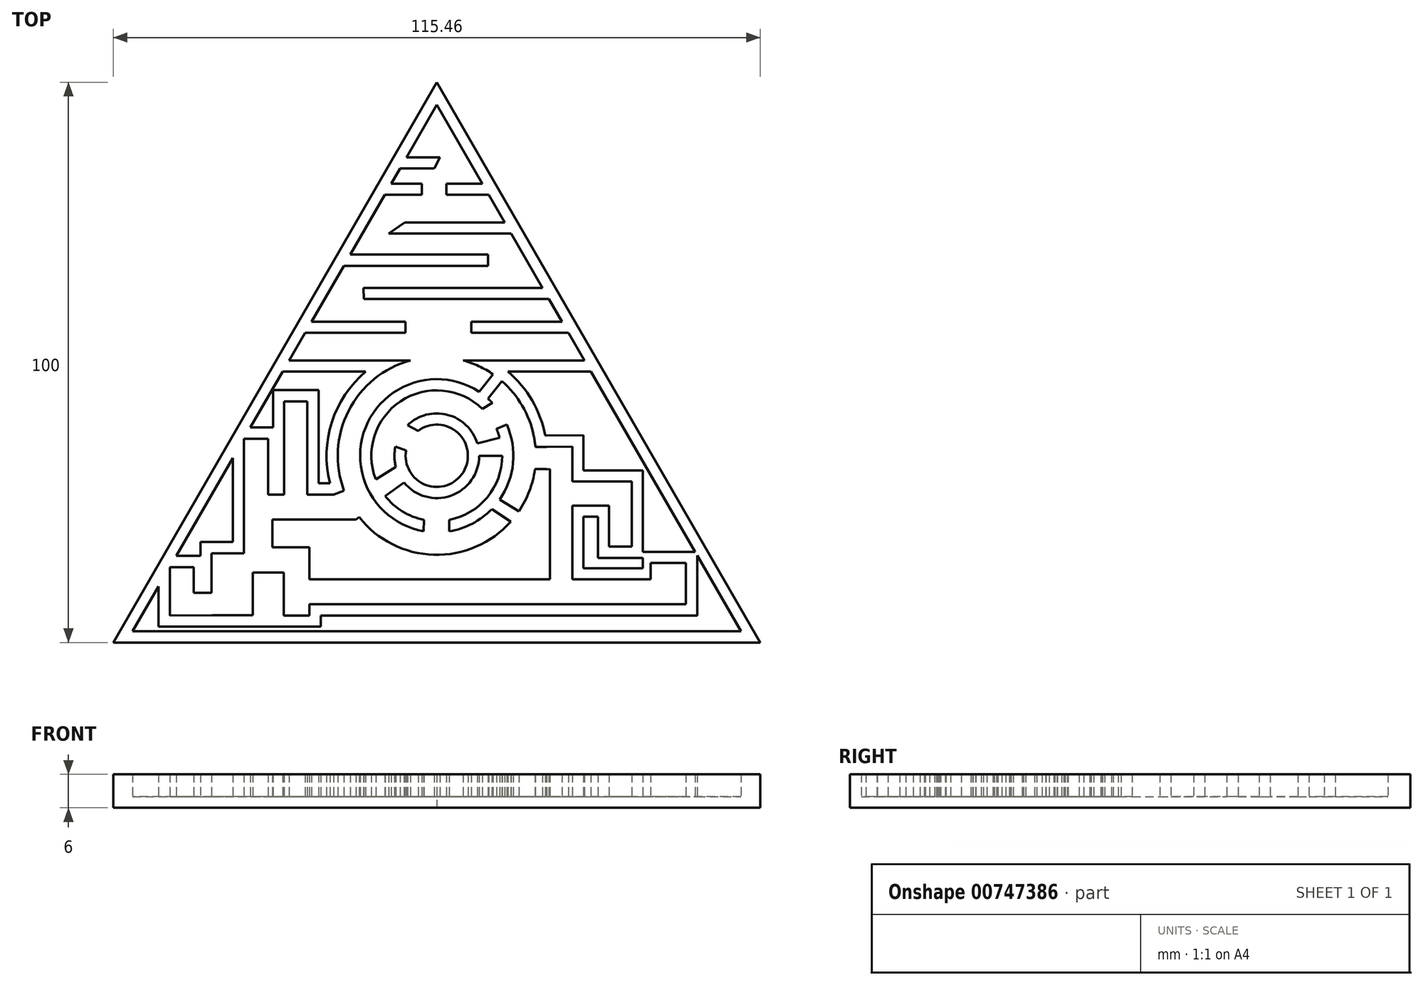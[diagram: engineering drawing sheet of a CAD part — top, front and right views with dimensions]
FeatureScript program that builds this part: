
annotation { "Feature Type Name" : "Feature", "Feature Type Description" : "" }
export const myFeature = defineFeature(function(context is Context, id is Id, definition is map)
    precondition{}
    {
        {
            var Q0;
            Q0=qCreatedBy(makeId("Top.planeOp"),FACE);
            var sketch = newSketch(context, id + "F0", { "sketchPlane" : qUnion([Q0])});
            skLineSegment(sketch, "E0.0", {"start": v(0, 66.66) * mm, "end": v(57.73, -33.34) * mm});
            skLineSegment(sketch, "E0.1", {"start": v(57.73, -33.34) * mm, "end": v(-57.73, -33.34) * mm});
            skLineSegment(sketch, "E0.2", {"start": v(-57.73, -33.34) * mm, "end": v(0, 66.66) * mm});
            skLineSegment(sketch, "E1.0", {"start": v(-54.26, -31.34) * mm, "end": v(-49.65, -23.35) * mm});
            skLineSegment(sketch, "E1.1", {"start": v(54.26, -31.34) * mm, "end": v(-54.26, -31.34) * mm});
            skLineSegment(sketch, "E1.2", {"start": v(0, 62.66) * mm, "end": v(8.12, 48.6) * mm});
            skLineSegment(sketch, "E2", {"start": v(-5.41, 53.28) * mm, "end": v(0.55, 53.28) * mm});
            skLineSegment(sketch, "E3.0", {"start": v(-5.31, 51.28) * mm, "end": v(-0.47, 51.28) * mm});
            skLineSegment(sketch, "E4", {"start": v(8.12, 48.6) * mm, "end": v(1.73, 48.6) * mm});
            skLineSegment(sketch, "E5", {"start": v(-2.68, 48.6) * mm, "end": v(-8.12, 48.6) * mm});
            skLineSegment(sketch, "E6.0", {"start": v(-2.68, 46.6) * mm, "end": v(-8.12, 46.6) * mm});
            skLineSegment(sketch, "E6.2", {"start": v(8.12, 46.6) * mm, "end": v(1.73, 46.6) * mm});
            skLineSegment(sketch, "E7", {"start": v(12.12, 41.67) * mm, "end": v(-5.72, 41.67) * mm});
            skLineSegment(sketch, "E8.0", {"start": v(12.06, 39.67) * mm, "end": v(-8.59, 39.67) * mm});
            skLineSegment(sketch, "E9", {"start": v(-15.45, 35.9) * mm, "end": v(9.13, 35.9) * mm});
            skLineSegment(sketch, "E10.0", {"start": v(-15.45, 33.9) * mm, "end": v(9.13, 33.9) * mm});
            skLineSegment(sketch, "E11", {"start": v(-15.45, 33.9) * mm, "end": v(-16.6, 33.9) * mm});
            skLineSegment(sketch, "E12", {"start": v(12.06, 39.67) * mm, "end": v(13.27, 39.67) * mm});
            skLineSegment(sketch, "E13", {"start": v(-8.59, 39.67) * mm, "end": v(-5.72, 41.67) * mm});
            skLineSegment(sketch, "E14", {"start": v(-2.68, 46.6) * mm, "end": v(-2.68, 48.6) * mm});
            skLineSegment(sketch, "E15", {"start": v(1.73, 48.6) * mm, "end": v(1.73, 46.6) * mm});
            skLineSegment(sketch, "E16", {"start": v(8.12, 46.6) * mm, "end": v(9.27, 46.6) * mm});
            skLineSegment(sketch, "E17", {"start": v(-8.12, 46.6) * mm, "end": v(-9.27, 46.6) * mm});
            skLineSegment(sketch, "E18", {"start": v(-5.31, 51.28) * mm, "end": v(-6.57, 51.28) * mm});
            skLineSegment(sketch, "E19", {"start": v(-0.47, 51.28) * mm, "end": v(0.55, 53.28) * mm});
            skLineSegment(sketch, "E20", {"start": v(9.13, 35.9) * mm, "end": v(9.13, 33.9) * mm});
            skLineSegment(sketch, "E21", {"start": v(18.87, 29.98) * mm, "end": v(-13.07, 29.98) * mm});
            skLineSegment(sketch, "E22.0", {"start": v(18.7, 27.98) * mm, "end": v(-13.01, 27.98) * mm});
            skLineSegment(sketch, "E23", {"start": v(-13.07, 29.98) * mm, "end": v(-13.01, 27.98) * mm});
            skLineSegment(sketch, "E24", {"start": v(18.7, 27.98) * mm, "end": v(20.02, 27.98) * mm});
            skArc(sketch, "E25", {"start": v(-4.71, 17.03) * mm, "mid": v(-7.07, 16.2) * mm, "end": v(-9.3, 15.03) * mm});
            skLineSegment(sketch, "E26", {"start": v(-22.35, 23.94) * mm, "end": v(-5.6, 23.94) * mm});
            skLineSegment(sketch, "E27", {"start": v(6.16, 23.94) * mm, "end": v(22.35, 23.94) * mm});
            skLineSegment(sketch, "E28.0", {"start": v(-22.35, 21.94) * mm, "end": v(-5.6, 21.94) * mm});
            skLineSegment(sketch, "E29.0", {"start": v(6.16, 21.94) * mm, "end": v(22.35, 21.94) * mm});
            skLineSegment(sketch, "E30", {"start": v(-5.6, 21.94) * mm, "end": v(-5.6, 23.94) * mm});
            skLineSegment(sketch, "E31", {"start": v(6.16, 23.94) * mm, "end": v(6.16, 21.94) * mm});
            skLineSegment(sketch, "E32", {"start": v(22.35, 21.94) * mm, "end": v(23.5, 21.94) * mm});
            skLineSegment(sketch, "E33", {"start": v(-22.35, 21.94) * mm, "end": v(-23.5, 21.94) * mm});
            skLineSegment(sketch, "E34", {"start": v(-26.34, 17.03) * mm, "end": v(-4.71, 17.03) * mm});
            skLineSegment(sketch, "E35", {"start": v(4.71, 17.03) * mm, "end": v(26.34, 17.03) * mm});
            skLineSegment(sketch, "E36.0", {"start": v(-26.34, 15.03) * mm, "end": v(-12.7, 15.03) * mm});
            skLineSegment(sketch, "E37.0", {"start": v(12.7, 15.03) * mm, "end": v(26.34, 15.03) * mm});
            skLineSegment(sketch, "E38", {"start": v(-26.34, 15.03) * mm, "end": v(-27.5, 15.03) * mm});
            skLineSegment(sketch, "E39", {"start": v(26.34, 15.03) * mm, "end": v(27.5, 15.03) * mm});
            skLineSegment(sketch, "E40.trimOffspring", {"start": v(-15.45, 35.9) * mm, "end": v(-9.27, 46.6) * mm});
            skLineSegment(sketch, "E41.trimOffspring", {"start": v(13.27, 39.67) * mm, "end": v(18.87, 29.98) * mm});
            skLineSegment(sketch, "E42.trimOffspring", {"start": v(20.02, 27.98) * mm, "end": v(22.35, 23.94) * mm});
            skLineSegment(sketch, "E43.trimOffspring", {"start": v(-26.34, 17.03) * mm, "end": v(-23.5, 21.94) * mm});
            skLineSegment(sketch, "E44.trimOffspring", {"start": v(-22.35, 23.94) * mm, "end": v(-16.6, 33.9) * mm});
            skLineSegment(sketch, "E45.trimOffspring", {"start": v(27.5, 15.03) * mm, "end": v(46.07, -17.15) * mm});
            skLineSegment(sketch, "E46.trimOffspring", {"start": v(23.5, 21.94) * mm, "end": v(26.34, 17.03) * mm});
            skLineSegment(sketch, "E47.trimOffspring", {"start": v(-8.12, 48.6) * mm, "end": v(-6.57, 51.28) * mm});
            skLineSegment(sketch, "E48.trimOffspring", {"start": v(9.27, 46.6) * mm, "end": v(12.12, 41.67) * mm});
            skLineSegment(sketch, "E49.trimOffspring", {"start": v(-5.41, 53.28) * mm, "end": v(0, 62.66) * mm});
            skArc(sketch, "E50.trimOffspring", {"start": v(9.3, 15.03) * mm, "mid": v(7.07, 16.2) * mm, "end": v(4.71, 17.03) * mm});
            skArc(sketch, "E51", {"start": v(-4.71, 17.03) * mm, "mid": v(-15.75, 8.02) * mm, "end": v(-16.54, -6.22) * mm});
            skArc(sketch, "E52.0", {"start": v(7.52, 11.42) * mm, "mid": v(-12.72, 5.03) * mm, "end": v(-2.32, -13.48) * mm});
            skArc(sketch, "E53.0", {"start": v(2.2, -11.47) * mm, "mid": v(9, -7.44) * mm, "end": v(11.67, 0) * mm});
            skArc(sketch, "E54.0", {"start": v(7.23, 2.22) * mm, "mid": v(1.91, 7.31) * mm, "end": v(-5.21, 5.47) * mm});
            skArc(sketch, "E55.0", {"start": v(-5.48, 0.95) * mm, "mid": v(4.73, -2.91) * mm, "end": v(-3.32, 4.46) * mm});
            skArc(sketch, "E56.0", {"start": v(-12.7, 15.03) * mm, "mid": v(-18.74, 5.98) * mm, "end": v(-19.05, -4.9) * mm});
            skLineSegment(sketch, "E57", {"start": v(7.52, 11.42) * mm, "end": v(10.06, 14.53) * mm});
            skLineSegment(sketch, "E58.0", {"start": v(10.67, 12.12) * mm, "end": v(11.63, 13.3) * mm});
            skLineSegment(sketch, "E59", {"start": v(10.67, 12.12) * mm, "end": v(9.13, 10.18) * mm});
            skArc(sketch, "E60.trimOffspring", {"start": v(10.06, 14.53) * mm, "mid": v(7.49, 16) * mm, "end": v(4.71, 17.03) * mm});
            skLineSegment(sketch, "E61.left", {"start": v(-2.32, -11.44) * mm, "end": v(-2.32, -13.48) * mm});
            skLineSegment(sketch, "E61.right", {"start": v(2.2, -11.47) * mm, "end": v(2.19, -13.5) * mm});
            skArc(sketch, "E62.trimOffspring", {"start": v(2.19, -13.5) * mm, "mid": v(6.32, -12.12) * mm, "end": v(9.82, -9.52) * mm});
            skLineSegment(sketch, "E63", {"start": v(-9.2, -7.18) * mm, "end": v(-5.86, -4.77) * mm});
            skLineSegment(sketch, "E64", {"start": v(-10.88, -4.22) * mm, "end": v(-7.3, -1.99) * mm});
            skLineSegment(sketch, "E65", {"start": v(7.23, 2.22) * mm, "end": v(11.23, 3.2) * mm});
            skLineSegment(sketch, "E66", {"start": v(7.56, 0) * mm, "end": v(11.67, 0) * mm});
            skArc(sketch, "E67.trimOffspring", {"start": v(11.23, 3.2) * mm, "mid": v(10.97, 4) * mm, "end": v(10.65, 4.79) * mm});
            skArc(sketch, "E68.trimOffspring", {"start": v(-5.86, -4.77) * mm, "mid": v(2.53, -7.12) * mm, "end": v(7.56, 0) * mm});
            skArc(sketch, "E69.trimOffspring", {"start": v(-9.2, -7.18) * mm, "mid": v(-6.14, -9.93) * mm, "end": v(-2.32, -11.44) * mm});
            skArc(sketch, "E70.trimOffspring", {"start": v(-13.87, -10.96) * mm, "mid": v(-0.52, -17.67) * mm, "end": v(13.2, -11.75) * mm});
            skLineSegment(sketch, "E71", {"start": v(-18.42, -6.9) * mm, "end": v(-16.54, -6.22) * mm});
            skLineSegment(sketch, "E72", {"start": v(-18.42, -6.9) * mm, "end": v(-23.1, -6.9) * mm});
            skLineSegment(sketch, "E73", {"start": v(-23.1, -6.9) * mm, "end": v(-23.1, 9.73) * mm});
            skLineSegment(sketch, "E74", {"start": v(-23.1, 9.73) * mm, "end": v(-27.23, 9.73) * mm});
            skLineSegment(sketch, "E75", {"start": v(-27.23, 9.73) * mm, "end": v(-27.23, -6.9) * mm});
            skLineSegment(sketch, "E76", {"start": v(-27.23, -6.9) * mm, "end": v(-30.11, -6.9) * mm});
            skLineSegment(sketch, "E77", {"start": v(-30.11, -6.9) * mm, "end": v(-30.11, 3.06) * mm});
            skLineSegment(sketch, "E78", {"start": v(-30.11, 3.06) * mm, "end": v(-34.4, 3.06) * mm});
            skLineSegment(sketch, "E79", {"start": v(-34.4, 3.06) * mm, "end": v(-34.4, -6.9) * mm});
            skLineSegment(sketch, "E80", {"start": v(-34.4, -6.9) * mm, "end": v(-34.4, -13.59) * mm});
            skLineSegment(sketch, "E81", {"start": v(-34.4, -13.59) * mm, "end": v(-34.4, -17.39) * mm});
            skLineSegment(sketch, "E82", {"start": v(-34.4, -17.39) * mm, "end": v(-40.19, -17.39) * mm});
            skLineSegment(sketch, "E83", {"start": v(-40.19, -17.39) * mm, "end": v(-40.19, -24.18) * mm});
            skLineSegment(sketch, "E84", {"start": v(-40.19, -24.18) * mm, "end": v(-40.19, -24.46) * mm});
            skLineSegment(sketch, "E85", {"start": v(-40.19, -24.46) * mm, "end": v(-43.4, -24.46) * mm});
            skLineSegment(sketch, "E86", {"start": v(-43.4, -24.46) * mm, "end": v(-43.4, -19.89) * mm});
            skLineSegment(sketch, "E87", {"start": v(-43.4, -19.89) * mm, "end": v(-47.65, -19.89) * mm});
            skLineSegment(sketch, "E88", {"start": v(-47.65, -19.89) * mm, "end": v(-47.65, -24.46) * mm});
            skLineSegment(sketch, "E89", {"start": v(-47.65, -24.46) * mm, "end": v(-47.65, -28.51) * mm});
            skLineSegment(sketch, "E90", {"start": v(-47.65, -28.51) * mm, "end": v(-40.09, -28.47) * mm});
            skLineSegment(sketch, "E91", {"start": v(-40.09, -28.47) * mm, "end": v(-32.84, -28.47) * mm});
            skLineSegment(sketch, "E92", {"start": v(-32.84, -28.47) * mm, "end": v(-32.84, -20.83) * mm});
            skLineSegment(sketch, "E93", {"start": v(-32.84, -20.83) * mm, "end": v(-27.33, -20.83) * mm});
            skLineSegment(sketch, "E94", {"start": v(-27.33, -20.83) * mm, "end": v(-27.33, -28.5) * mm});
            skLineSegment(sketch, "E95", {"start": v(-27.33, -28.5) * mm, "end": v(-22.71, -28.5) * mm});
            skLineSegment(sketch, "E96", {"start": v(-22.71, -28.5) * mm, "end": v(-22.71, -26.53) * mm});
            skLineSegment(sketch, "E97", {"start": v(-22.71, -20.74) * mm, "end": v(-22.71, -16.35) * mm});
            skLineSegment(sketch, "E98", {"start": v(-22.71, -16.35) * mm, "end": v(-29.3, -16.35) * mm});
            skLineSegment(sketch, "E99", {"start": v(-29.3, -16.35) * mm, "end": v(-29.3, -11.37) * mm});
            skLineSegment(sketch, "E100", {"start": v(-29.3, -11.37) * mm, "end": v(-24.62, -11.37) * mm});
            skLineSegment(sketch, "E101", {"start": v(-14.4, -11.37) * mm, "end": v(-13.87, -10.96) * mm});
            skLineSegment(sketch, "E102.0", {"start": v(-21.1, -4.9) * mm, "end": v(-21.1, 9.73) * mm});
            skLineSegment(sketch, "E103.0", {"start": v(-23.1, 11.73) * mm, "end": v(-27.23, 11.73) * mm});
            skLineSegment(sketch, "E104.top", {"start": v(-23.1, 11.71) * mm, "end": v(-21.11, 11.71) * mm});
            skLineSegment(sketch, "E104.right", {"start": v(-21.11, 9.73) * mm, "end": v(-21.11, 11.71) * mm});
            skLineSegment(sketch, "E105.0", {"start": v(-29.23, 9.73) * mm, "end": v(-29.23, 5.06) * mm});
            skLineSegment(sketch, "E106.top", {"start": v(-29.23, 11.73) * mm, "end": v(-27.23, 11.73) * mm});
            skLineSegment(sketch, "E106.left", {"start": v(-29.23, 9.73) * mm, "end": v(-29.23, 11.73) * mm});
            skLineSegment(sketch, "E107.0", {"start": v(-30.11, 5.06) * mm, "end": v(-33.25, 5.06) * mm});
            skLineSegment(sketch, "E108.bottom", {"start": v(-30.11, 5.06) * mm, "end": v(-29.23, 5.06) * mm});
            skLineSegment(sketch, "E109.trimOffspring", {"start": v(-33.25, 5.06) * mm, "end": v(-27.5, 15.03) * mm});
            skLineSegment(sketch, "E110.0", {"start": v(-36.4, -13.59) * mm, "end": v(-36.4, -15.39) * mm});
            skLineSegment(sketch, "E110.1", {"start": v(-36.4, -6.9) * mm, "end": v(-36.4, -13.59) * mm});
            skLineSegment(sketch, "E110.2", {"start": v(-36.4, -0.4) * mm, "end": v(-36.4, -6.9) * mm});
            skLineSegment(sketch, "E111.0", {"start": v(-36.4, -15.39) * mm, "end": v(-40.19, -15.39) * mm});
            skLineSegment(sketch, "E112.0", {"start": v(-42.19, -17.39) * mm, "end": v(-42.19, -17.89) * mm});
            skLineSegment(sketch, "E113.top", {"start": v(-42.19, -15.39) * mm, "end": v(-40.19, -15.39) * mm});
            skLineSegment(sketch, "E113.left", {"start": v(-42.19, -17.39) * mm, "end": v(-42.19, -15.39) * mm});
            skLineSegment(sketch, "E114.0", {"start": v(-43.4, -17.89) * mm, "end": v(-46.5, -17.89) * mm});
            skLineSegment(sketch, "E115.bottom", {"start": v(-43.4, -17.89) * mm, "end": v(-42.19, -17.89) * mm});
            skLineSegment(sketch, "E116.0", {"start": v(-49.65, -24.46) * mm, "end": v(-49.65, -28.51) * mm});
            skLineSegment(sketch, "E116.1", {"start": v(-49.65, -23.35) * mm, "end": v(-49.65, -24.46) * mm});
            skLineSegment(sketch, "E117.trimOffspring", {"start": v(-46.5, -17.89) * mm, "end": v(-36.4, -0.4) * mm});
            skLineSegment(sketch, "E118.0", {"start": v(-47.64, -30.5) * mm, "end": v(-40.07, -30.47) * mm});
            skLineSegment(sketch, "E119.bottom", {"start": v(-47.65, -28.51) * mm, "end": v(-47.64, -28.51) * mm});
            skLineSegment(sketch, "E119.top", {"start": v(-49.65, -30.5) * mm, "end": v(-47.64, -30.5) * mm});
            skLineSegment(sketch, "E119.left", {"start": v(-49.65, -28.51) * mm, "end": v(-49.65, -30.5) * mm});
            skLineSegment(sketch, "E120.0", {"start": v(-40.09, -30.47) * mm, "end": v(-32.84, -30.47) * mm});
            skLineSegment(sketch, "E121", {"start": v(-32.84, -30.47) * mm, "end": v(-27.36, -30.47) * mm});
            skLineSegment(sketch, "E122", {"start": v(-27.36, -30.47) * mm, "end": v(-20.88, -30.47) * mm});
            skLineSegment(sketch, "E123.top", {"start": v(-20.88, -30.47) * mm, "end": v(-20.72, -30.47) * mm});
            skLineSegment(sketch, "E123.right", {"start": v(-20.72, -28.5) * mm, "end": v(-20.72, -30.47) * mm});
            skLineSegment(sketch, "E124.0", {"start": v(-19.05, -4.9) * mm, "end": v(-21.1, -4.9) * mm});
            skLineSegment(sketch, "E125", {"start": v(-24.62, -11.37) * mm, "end": v(-20.71, -11.37) * mm});
            skLineSegment(sketch, "E126", {"start": v(-20.7, -13.37) * mm, "end": v(-20.7, -13.37) * mm});
            skPoint(sketch, "E126.endSnap0", {"position": v(-20.7, -13.3) * mm});
            skLineSegment(sketch, "E127", {"start": v(-20.71, -11.37) * mm, "end": v(-14.4, -11.37) * mm});
            skPoint(sketch, "E128.end.orphan", {"position": v(-20.67, -12.27) * mm});
            skLineSegment(sketch, "E129.bottom", {"start": v(-22.71, -22.05) * mm, "end": v(-20.71, -22.05) * mm});
            skLineSegment(sketch, "E129.top", {"start": v(-22.71, -26.53) * mm, "end": v(-20.71, -26.53) * mm});
            skLineSegment(sketch, "E130.trimOffspring", {"start": v(-22.71, -22.05) * mm, "end": v(-22.71, -20.74) * mm});
            skLineSegment(sketch, "E131", {"start": v(-20.71, -26.53) * mm, "end": v(-12.97, -26.53) * mm});
            skLineSegment(sketch, "E132.0", {"start": v(-20.71, -28.53) * mm, "end": v(-12.97, -28.53) * mm});
            skLineSegment(sketch, "E133", {"start": v(-20.71, -22.05) * mm, "end": v(-12.69, -22.05) * mm});
            skLineSegment(sketch, "E134", {"start": v(9.82, -9.52) * mm, "end": v(13.2, -11.75) * mm});
            skLineSegment(sketch, "E135", {"start": v(14.65, -9.89) * mm, "end": v(11.23, -7.8) * mm});
            skLineSegment(sketch, "E136", {"start": v(-12.97, -28.53) * mm, "end": v(18.13, -28.53) * mm});
            skLineSegment(sketch, "E137.0", {"start": v(-12.97, -26.53) * mm, "end": v(18.13, -26.53) * mm});
            skLineSegment(sketch, "E138.0", {"start": v(-12.69, -22.05) * mm, "end": v(18.13, -22.05) * mm});
            skLineSegment(sketch, "E139", {"start": v(18.13, -26.53) * mm, "end": v(24.45, -26.53) * mm});
            skLineSegment(sketch, "E140", {"start": v(24.45, -26.53) * mm, "end": v(44.46, -26.53) * mm});
            skLineSegment(sketch, "E141", {"start": v(44.46, -26.53) * mm, "end": v(44.46, -19.15) * mm});
            skLineSegment(sketch, "E142", {"start": v(44.46, -19.15) * mm, "end": v(38.16, -19.15) * mm});
            skLineSegment(sketch, "E143", {"start": v(38.16, -19.15) * mm, "end": v(38.16, -22.05) * mm});
            skLineSegment(sketch, "E144", {"start": v(38.16, -22.05) * mm, "end": v(24.18, -22.05) * mm});
            skLineSegment(sketch, "E145", {"start": v(18.13, -28.53) * mm, "end": v(46.46, -28.53) * mm});
            skLineSegment(sketch, "E146.0", {"start": v(46.46, -26.53) * mm, "end": v(46.46, -19.15) * mm});
            skLineSegment(sketch, "E147", {"start": v(46.46, -26.53) * mm, "end": v(46.46, -28.53) * mm});
            skLineSegment(sketch, "E148.0", {"start": v(44.46, -17.15) * mm, "end": v(38.16, -17.15) * mm});
            skLineSegment(sketch, "E149.bottom", {"start": v(44.46, -17.15) * mm, "end": v(46.07, -17.15) * mm});
            skLineSegment(sketch, "E149.right", {"start": v(46.46, -17.82) * mm, "end": v(46.46, -19.15) * mm});
            skLineSegment(sketch, "E150.trimOffspring", {"start": v(46.46, -17.82) * mm, "end": v(54.26, -31.34) * mm});
            skLineSegment(sketch, "E151.top", {"start": v(36.8, -17.15) * mm, "end": v(38.16, -17.15) * mm});
            skLineSegment(sketch, "E151.right", {"start": v(38.16, -20.05) * mm, "end": v(38.16, -19.15) * mm});
            skLineSegment(sketch, "E152.left", {"start": v(20.18, -20.05) * mm, "end": v(20.18, -22.05) * mm});
            skLineSegment(sketch, "E152.right", {"start": v(24.18, -20.05) * mm, "end": v(24.18, -22.05) * mm});
            skLineSegment(sketch, "E153.trimOffspring", {"start": v(24.18, -20.05) * mm, "end": v(24.18, -20.05) * mm});
            skLineSegment(sketch, "E154.trimOffspring", {"start": v(20.18, -22.05) * mm, "end": v(18.13, -22.05) * mm});
            skLineSegment(sketch, "E155", {"start": v(20.18, -20.05) * mm, "end": v(20.18, -6.8) * mm});
            skLineSegment(sketch, "E156", {"start": v(20.18, -6.8) * mm, "end": v(20.18, -2.4) * mm});
            skLineSegment(sketch, "E157", {"start": v(20.18, -2.4) * mm, "end": v(19.53, -2.4) * mm});
            skLineSegment(sketch, "E158.0", {"start": v(24.18, 1.65) * mm, "end": v(19.6, 1.6) * mm});
            skLineSegment(sketch, "E158.1", {"start": v(24.18, -4.6) * mm, "end": v(24.18, 1.65) * mm});
            skLineSegment(sketch, "E158.2", {"start": v(24.18, -20.05) * mm, "end": v(24.18, -8.9) * mm});
            skLineSegment(sketch, "E159.0", {"start": v(26.18, 3.68) * mm, "end": v(19.46, 3.6) * mm});
            skLineSegment(sketch, "E159.1", {"start": v(26.18, -2.6) * mm, "end": v(26.18, 3.68) * mm});
            skLineSegment(sketch, "E160", {"start": v(19.46, 3.6) * mm, "end": v(19.34, 3.6) * mm});
            skArc(sketch, "E161.trimOffspring", {"start": v(19.34, 3.6) * mm, "mid": v(17, 9.9) * mm, "end": v(12.7, 15.03) * mm});
            skLineSegment(sketch, "E162.top", {"start": v(19.6, 3.6) * mm, "end": v(19.34, 3.6) * mm});
            skArc(sketch, "E163.trimOffspring", {"start": v(17.3, 3.6) * mm, "mid": v(15.26, 8.92) * mm, "end": v(11.63, 13.3) * mm});
            skLineSegment(sketch, "E164", {"start": v(19.6, 1.6) * mm, "end": v(17.6, 1.6) * mm});
            skArc(sketch, "E165.trimOffspring", {"start": v(19.53, -2.4) * mm, "mid": v(19.53, -2.4) * mm, "end": v(19.53, -2.4) * mm});
            skLineSegment(sketch, "E166.bottom", {"start": v(20.18, -2.4) * mm, "end": v(17.51, -2.4) * mm});
            skLineSegment(sketch, "E166.top", {"start": v(20.18, 1.6) * mm, "end": v(17.6, 1.6) * mm});
            skArc(sketch, "E167", {"start": v(17.6, 1.6) * mm, "mid": v(17.48, 2.6) * mm, "end": v(17.3, 3.6) * mm});
            skArc(sketch, "E168.trimOffspring", {"start": v(8.13, 8.38) * mm, "mid": v(-6.45, 9.73) * mm, "end": v(-10.88, -4.22) * mm});
            skArc(sketch, "E169.trimOffspring", {"start": v(9.91, 9.42) * mm, "mid": v(9.53, 9.8) * mm, "end": v(9.13, 10.18) * mm});
            skLineSegment(sketch, "E170", {"start": v(10.65, 4.79) * mm, "end": v(12.5, 5.54) * mm});
            skLineSegment(sketch, "E171", {"start": v(9.91, 9.42) * mm, "end": v(8.13, 8.38) * mm});
            skLineSegment(sketch, "E172.bottom", {"start": v(24.18, -4.6) * mm, "end": v(34.8, -4.6) * mm});
            skLineSegment(sketch, "E172.top", {"start": v(24.18, -8.9) * mm, "end": v(30.76, -8.9) * mm});
            skLineSegment(sketch, "E173.top", {"start": v(34.8, -16.21) * mm, "end": v(30.76, -16.21) * mm});
            skLineSegment(sketch, "E173.left", {"start": v(34.8, -8.9) * mm, "end": v(34.8, -16.21) * mm});
            skLineSegment(sketch, "E173.right", {"start": v(30.76, -8.9) * mm, "end": v(30.76, -16.21) * mm});
            skLineSegment(sketch, "E174.0", {"start": v(36.8, -8.9) * mm, "end": v(36.8, -16.21) * mm});
            skLineSegment(sketch, "E175.right", {"start": v(36.8, -17.15) * mm, "end": v(36.8, -16.21) * mm});
            skLineSegment(sketch, "E176", {"start": v(34.8, -4.6) * mm, "end": v(34.8, -8.9) * mm});
            skLineSegment(sketch, "E177.0", {"start": v(36.8, -2.6) * mm, "end": v(36.8, -8.9) * mm});
            skLineSegment(sketch, "E177.1", {"start": v(26.18, -2.6) * mm, "end": v(36.8, -2.6) * mm});
            skArc(sketch, "E178.trimOffspring", {"start": v(-7.38, 1.64) * mm, "mid": v(-7.56, -0.18) * mm, "end": v(-7.3, -1.99) * mm});
            skLineSegment(sketch, "E179", {"start": v(-7.38, 1.64) * mm, "end": v(-5.48, 0.95) * mm});
            skLineSegment(sketch, "E180", {"start": v(-3.32, 4.46) * mm, "end": v(-5.21, 5.47) * mm});
            skPoint(sketch, "E181.start.orphan", {"position": v(-20.71, -14.35) * mm});
            skArc(sketch, "E182.trimOffspring", {"start": v(14.65, -9.89) * mm, "mid": v(16.51, -6.3) * mm, "end": v(17.51, -2.4) * mm});
            skArc(sketch, "E183.trimOffspring", {"start": v(11.23, -7.8) * mm, "mid": v(13.61, -1.3) * mm, "end": v(12.5, 5.54) * mm});
            skLineSegment(sketch, "E184", {"start": v(-21.11, 9.73) * mm, "end": v(-21.1, 9.73) * mm});
            skLineSegment(sketch, "E185", {"start": v(-23.1, 11.73) * mm, "end": v(-23.1, 11.71) * mm});
            skLineSegment(sketch, "E186", {"start": v(-20.71, -28.53) * mm, "end": v(-20.72, -28.5) * mm});
            skLineSegment(sketch, "E187.0", {"start": v(26.18, -10.9) * mm, "end": v(28.76, -10.9) * mm});
            skLineSegment(sketch, "E187.1", {"start": v(26.18, -20.05) * mm, "end": v(26.18, -10.9) * mm});
            skLineSegment(sketch, "E188.0", {"start": v(36.8, -20.05) * mm, "end": v(26.18, -20.05) * mm});
            skLineSegment(sketch, "E189.0", {"start": v(34.8, -18.21) * mm, "end": v(30.76, -18.21) * mm});
            skLineSegment(sketch, "E190.0", {"start": v(28.76, -10.9) * mm, "end": v(28.76, -16.21) * mm});
            skLineSegment(sketch, "E191.top", {"start": v(28.76, -18.21) * mm, "end": v(30.76, -18.21) * mm});
            skLineSegment(sketch, "E191.left", {"start": v(28.76, -16.21) * mm, "end": v(28.76, -18.21) * mm});
            skLineSegment(sketch, "E192", {"start": v(34.8, -18.21) * mm, "end": v(36.8, -18.21) * mm});
            skLineSegment(sketch, "E193", {"start": v(36.8, -18.21) * mm, "end": v(36.8, -20.05) * mm});
            skSolve(sketch);
        }
        {
            var Q0;
            Q0 = qSketchRegion(id + "F0", true);
            extrude(context, id + "F1", {"entities" : qUnion([Q0]), "depth" : 4 * mm, "offsetDistance" : 25 * mm});
        }
        {
            var Q0;
            Q0=qCreatedBy(makeId("Top.planeOp"),FACE);
            var sketch = newSketch(context, id + "F2", { "sketchPlane" : qUnion([Q0])});
            skLineSegment(sketch, "E194.0", {"start": v(57.73, -33.34) * mm, "end": v(-57.73, -33.34) * mm});
            skLineSegment(sketch, "E195.0", {"start": v(-57.73, -33.34) * mm, "end": v(0, 66.66) * mm});
            skLineSegment(sketch, "E196.0", {"start": v(0, 66.66) * mm, "end": v(57.73, -33.34) * mm});
            skSolve(sketch);
        }
        {
            var Q0;
            Q0 = qSketchRegion(id + "F2", true);
            extrude(context, id + "F3", {"entities" : qUnion([Q0]), "operationType" : NewBodyOperationType.ADD, "oppositeDirection" : true, "depth" : 2 * mm, "offsetDistance" : 25 * mm});
        }
    });
